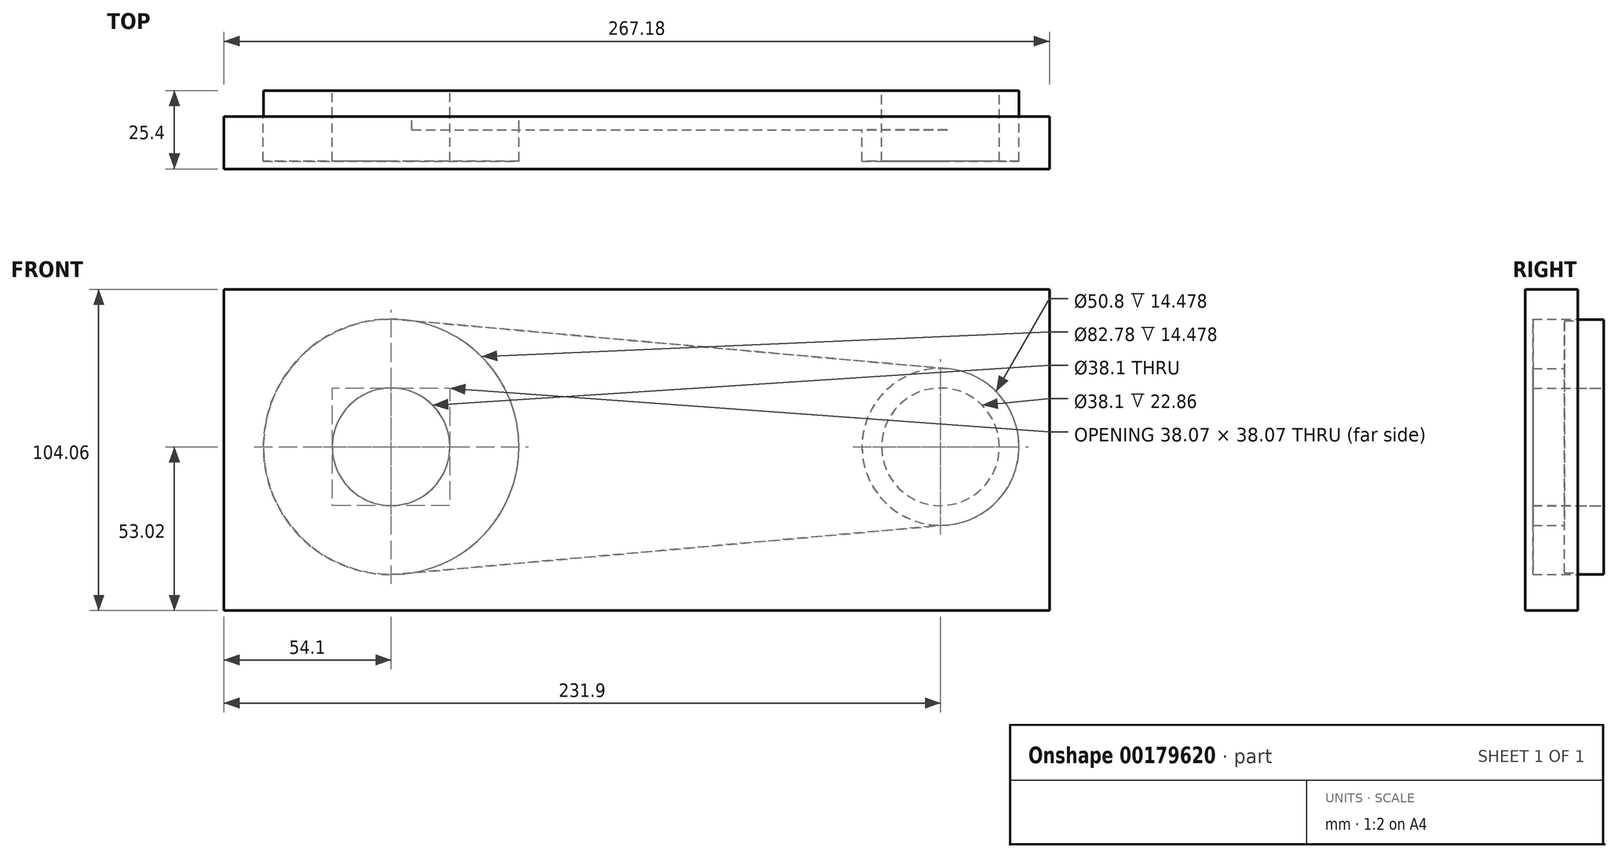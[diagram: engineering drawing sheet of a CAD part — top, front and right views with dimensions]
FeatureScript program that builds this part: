
annotation { "Feature Type Name" : "Feature", "Feature Type Description" : "" }
export const myFeature = defineFeature(function(context is Context, id is Id, definition is map)
    precondition{}
    {
        {
            var Q0;
            Q0=qCreatedBy(makeId("Front.planeOp"),FACE);
            var sketch = newSketch(context, id + "F0", { "sketchPlane" : qUnion([Q0])});
            skCircle(sketch, "E0", {"center": v(0, 0) * mm, "radius": 41.28 * mm});
            skCircle(sketch, "E1", {"center": v(177.8, 0) * mm, "radius": 25.4 * mm});
            skLineSegment(sketch, "E2", {"start": v(0, 0) * mm, "end": v(177.8, 0) * mm, "construction": true});
            skLineSegment(sketch, "E3", {"start": v(3.69, 41.11) * mm, "end": v(180.07, 25.3) * mm});
            skLineSegment(sketch, "E4.MirrorCS", {"start": v(3.69, -41.11) * mm, "end": v(180.07, -25.3) * mm});
            skLineSegment(sketch, "E5", {"start": v(0, 0) * mm, "end": v(192.72, 0) * mm, "construction": true});
            skCircle(sketch, "E6", {"center": v(0, 0) * mm, "radius": 19.05 * mm});
            skCircle(sketch, "E7", {"center": v(177.8, 0) * mm, "radius": 19.05 * mm});
            skSolve(sketch);
        }
        {
            var Q0;
            {var subQ0=sQuery(id+"F0.wireOp",EDGE,"E3");Q0=makeQuery(id+"F0.imprint","IMPRINT",FACE,{"disambiguationData":[TD([[makeQuery(id+"F0.imprint","IMPRINT",EDGE,{"derivedFrom":subQ0}),-1.0]])]});}
            extrude(context, id + "F1", {"entities" : qUnion([Q0]), "offsetDistance" : 25.4 * mm, "depth" : 12.7 * mm});
        }
        {
            var Q0;
            Q0=makeQuery(id+"F0.imprint","IMPRINT",FACE,{"disambiguationData":[TD([[makeQuery(id+"F0.imprint","IMPRINT",EDGE,{"derivedFrom":sQuery(id+"F0.wireOp",EDGE,"E6")}),-1.0]])]});
            var Q1;
            Q1=makeQuery(id+"F0.imprint","IMPRINT",FACE,{"disambiguationData":[TD([[makeQuery(id+"F0.imprint","IMPRINT",EDGE,{"derivedFrom":sQuery(id+"F0.wireOp",EDGE,"E7")}),-1.0]])]});
            extrude(context, id + "F2", {"entities" : qUnion([Q0, Q1]), "operationType" : NewBodyOperationType.ADD, "offsetDistance" : 25.4 * mm, "depth" : 22.86 * mm});
        }
        {
            var Q0;
            Q0=makeQuery(id+"F2.opExtrude","CAP_EDGE",EDGE,{"disambiguationData":[OSD([sQuery(id+"F0.wireOp",EDGE,"E0")])],"isStart":false});
            chamfer(context, id + "F3", {"entities" : qUnion([Q0]), "width" : 6.35 * mm, "tangentPropagation" : true});
        }
        {
            var Q0;
            Q0=qCreatedBy(makeId("Front.planeOp"),FACE);
            var sketch = newSketch(context, id + "F4", { "sketchPlane" : qUnion([Q0])});
            skLineSegment(sketch, "E8.bottom", {"start": v(-54.1, -53.02) * mm, "end": v(213.08, -53.02) * mm});
            skLineSegment(sketch, "E8.top", {"start": v(-54.1, 51.04) * mm, "end": v(213.08, 51.04) * mm});
            skLineSegment(sketch, "E8.left", {"start": v(-54.1, -53.02) * mm, "end": v(-54.1, 51.04) * mm});
            skLineSegment(sketch, "E8.right", {"start": v(213.08, -53.02) * mm, "end": v(213.08, 51.04) * mm});
            skSolve(sketch);
        }
        {
            var Q0;
            Q0=makeQuery(id+"F4.imprint","IMPRINT",FACE,{"disambiguationData":[TD([[makeQuery(id+"F4.imprint","IMPRINT",EDGE,{"derivedFrom":sQuery(id+"F4.wireOp",EDGE,"E8.bottom")}),1.0]])]});
            extrude(context, id + "F5", {"entities" : qUnion([Q0]), "depth" : 25.4 * mm, "offsetDistance" : 25.4 * mm, "hasSecondDirection" : true, "secondDirectionOppositeDirection" : false, "secondDirectionDepth" : 8.38 * mm});
        }
        {
            var Q0;
            Q0=makeQuery(id+"F1.opExtrude","SWEPT_BODY",BODY,{"disambiguationData":[OSD([sQuery(id+"F0.wireOp",EDGE,"E0"),sQuery(id+"F0.wireOp",EDGE,"E1"),sQuery(id+"F0.wireOp",EDGE,"E3"),sQuery(id+"F0.wireOp",EDGE,"E4.MirrorCS")])]});
            var Q1;
            Q1=makeQuery(id+"F5.opExtrude","SWEPT_BODY",BODY,{"disambiguationData":[OSD([sQuery(id+"F4.wireOp",EDGE,"E8.bottom"),sQuery(id+"F4.wireOp",EDGE,"E8.top"),sQuery(id+"F4.wireOp",EDGE,"E8.left"),sQuery(id+"F4.wireOp",EDGE,"E8.right")])]});
            booleanBodies(context, id + "F6", {"operationType" : BooleanOperationType.SUBTRACTION, "tools" : qUnion([Q0]), "targets" : qUnion([Q1]), "keepTools" : true});
        }
        {
            var Q0;
            Q0=makeQuery(id+"F6.opBoolean","SPLIT",FACE,{"disambiguationData":[TD([makeQuery(id+"F2.opExtrude","SWEPT_FACE",FACE,{"disambiguationData":[OSD([sQuery(id+"F0.wireOp",EDGE,"E6")])]})])],"derivedFrom":makeQuery(id+"F5.opExtrude","CAP_FACE",FACE,{"disambiguationData":[OSD([sQuery(id+"F4.wireOp",EDGE,"E8.bottom"),sQuery(id+"F4.wireOp",EDGE,"E8.top"),sQuery(id+"F4.wireOp",EDGE,"E8.left"),sQuery(id+"F4.wireOp",EDGE,"E8.right")])],"isStart":true})});
            var sketch = newSketch(context, id + "F7", { "sketchPlane" : qUnion([Q0])});
            skCircle(sketch, "E9", {"center": v(0, 0) * mm, "radius": 19.04 * mm});
            skCircle(sketch, "E10.0", {"center": v(0, 0) * mm, "radius": 41.39 * mm});
            skSolve(sketch);
        }
        {
            var Q0;
            Q0 = qSketchRegion(id + "F7", true);
            var Q1;
            Q1=makeQuery(id+"F6.opBoolean","COPY",FACE,{"derivedFrom":makeQuery(id+"F2.opExtrude","CAP_FACE",FACE,{"disambiguationData":[OSD([sQuery(id+"F0.wireOp",EDGE,"E0"),sQuery(id+"F0.wireOp",EDGE,"E6")])],"isStart":false})});
            extrude(context, id + "F8", {"entities" : qUnion([Q0]), "operationType" : NewBodyOperationType.REMOVE, "endBound" : BoundingType.UP_TO_SURFACE, "oppositeDirection" : true, "depth" : 16.5 * mm, "endBoundEntityFace" : qUnion([Q1]), "offsetDistance" : 25.4 * mm});
        }
    });
